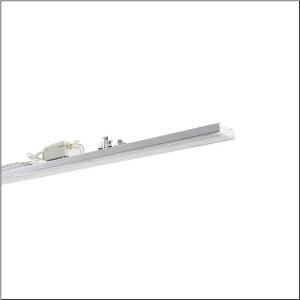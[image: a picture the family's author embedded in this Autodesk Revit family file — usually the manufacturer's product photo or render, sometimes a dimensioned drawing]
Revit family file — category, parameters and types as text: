
# Revit family: licross_21_recessed_mo_52tl19dv4e5g
name_source: partatom
category: Lighting Fixtures
units: mm (PartAtom-declared; Revit-internal decimal feet)

## family parameters
Cut with Voids When Loaded = No
Host = Face
Light Source = No
Part Type = Normal
Room Calculation Point = No
Round Connector Dimension = Use Diameter
Shared = No

## types (1)
- --- (1 x LED, 14780 lm, 85.3 W, 4000K)
    Apparent Load = 85 VA
    CIE Flux Codes = 55 90 98 100 100
    Color Rendering = 80
    Color Temperature = 4000K
    Default Elevation = 1800 mm
    Description = Licross 21 Recessed MO, luminaire insert, of sheet steel, galvanised, coil coated, white, length: 2.250mm, width: 66mm, height: 67mm, LED rated luminous flux: 14.780lm, light colour: 840, SDCM (Standard Deviation of Colour Matching)MacAdam ≤ 3 SDCM (initial), control gear: DALI 2, with plug, 5-pole, with phase selection, mains connection: 220..240V, AC, 50/60Hz, rated input power: 85W, internal wiring halogen-free, primary light control with lens, of plastic, primary optical cover: cover, of PMMA, light emission: direct distribution, primary light characteristic: double asymmetric, protection rating (complete): IP40, insulation class (complete): insulation class I (protective earthing), certification: CE, ENEC, VDE, UKCA, protection symbol: D if used in an environment without relevant dust loads with corresponding accessories, impact resistance: IK06, permissible ambient temperature for indoor applications: -25..+35°C, corresponds to IFS (International Featured Standards) requirements for safety and quality in the food industry, reducing of maximum allowable ambient temperature of 5°C with ceiling mounting, LABS conformity tested according to VDMA 24364:2018-05, The light source and the operating device comply with the requirements of the Ecodesign Regulation (EU) 2019/2020 and are replaceable in accordance with this regulation, packaging unit: 1 piece
    Height = 58 mm
    Lamp = 1 x LED
    Lamp Light Flux = 14780 lm
    Lamp Power = 85.3 W
    Lamp count = 1
    Length = 2250 mm
    Luminous efficacy = 173 lm/W
    Manufacturer = Siteco
    ModVariant = No
    Model = 52TL19DV4E5G
    Mounting Place = Ceiling
    Mounting Type = Pendant
    Number of Poles = 1
    OnlyDefault = Yes
    Power Factor = 1
    Product Name = Licross 21 Recessed MO
    Product group = luminaire insert | ceiling pendant
    ProductGroupID = 901
    Protection Class = Protection class I
    Protection Degree = IP 40
    RLX_Detail_Level = 1
    RLX_Emergency_Light_Flux = 0 lm
    RLX_Emergency_Type = 0
    RLX_Emergency_Type_DB = No
    RlxData = <blob elided: 29713 chars, md5=2f403fe8>
    Socket = socket
    Standby Power = 0 W
    System Light Flux = 14780 lm
    System Power = 85 W
    Type Comments = factory setting: luminous flux: 100 % | dim-lin: 254 | 390 mA
    Type Image = l_1296930.jpg
    URL = http://relux.com
    VarID = @adj_129773
    Voltage = 0 V
    Weight = 0.00 kg
    Width = 66 mm

## geometry (parser evidence)
native form markers: Blend x4, Sweep x10
no freeform markers — native parametric forms only
